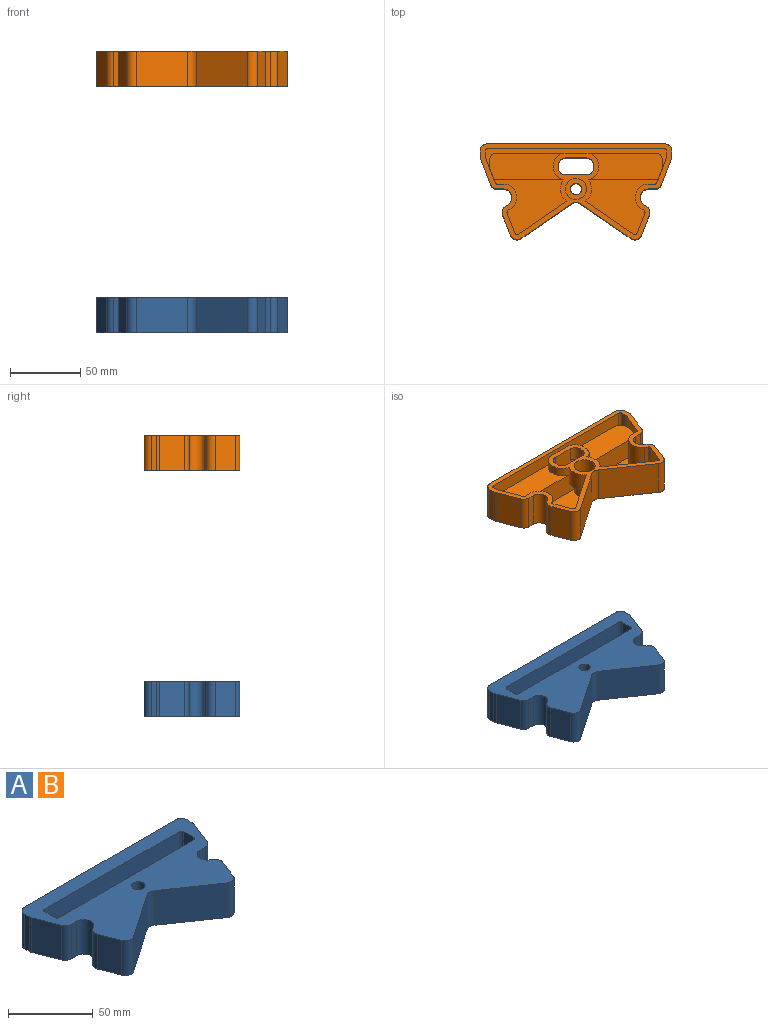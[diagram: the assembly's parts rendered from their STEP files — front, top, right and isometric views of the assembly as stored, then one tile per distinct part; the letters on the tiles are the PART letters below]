
ASSEMBLY  parts=2 mates=2
PART A: 100 faces, bbox 136x67.9x25 mm
  f0: plane 136x67.94mm, normal (0,0,-1), area 1747.5mm2, adj f3,f5,f6,f7,f8,f9,f11,f14
  f1: plane 50.5x12mm, normal (0,0,1), area 555mm2, adj f9,f10,f11,f39,f40,f42,f44,f46
  f2: cylinder r=4mm len=15mm, axis (0,0,-1), area 377mm2, adj f4,f36
  f3: plane 25x4.48mm, normal (0,-1,0), area 111.9mm2, adj f0,f4,f20,f28
  f4: plane 136x67.94mm, normal (0,0,1), area 5083.1mm2, adj f2,f3,f5,f6,f7,f8,f9,f10
  f5: plane 25x4.48mm, normal (0,-1,0), area 111.9mm2, adj f0,f4,f18,f25
  f6: plane 25x4.05mm, normal (1,0,0), area 101.4mm2, adj f0,f4,f31,f33
  f7: plane 126x25mm, normal (0,1,0), area 3150mm2, adj f0,f4,f33,f34
  f8: plane 25x4.05mm, normal (-1,0,0), area 101.4mm2, adj f0,f4,f32,f34
  f9: plane 112x25mm, normal (0,1,0), area 1830mm2, adj f0,f1,f4,f13,f38,f40,f45,f46
  f10: plane 15x8mm, normal (-1,0,0), area 120mm2, adj f1,f4,f39,f40
  f11: plane 112x25mm, normal (0,-1,0), area 1830mm2, adj f0,f1,f4,f13,f37,f39,f43,f44
  f12: plane 15x8mm, normal (1,0,0), area 120mm2, adj f4,f13,f37,f38
  f13: plane 50.5x12mm, normal (0,0,1), area 555mm2, adj f9,f11,f12,f37,f38,f41,f43,f45
  f14: plane 25x2.23mm, normal (-0.57,0.82,0), area 67.8mm2, adj f0,f4,f18,f26
  f15: plane 35.62x25mm, normal (0.57,-0.82,0), area 1081mm2, adj f0,f4,f19,f27
  f16: plane 35.62x25mm, normal (-0.57,-0.82,0), area 1081mm2, adj f0,f4,f19,f29
  f17: plane 25x2.23mm, normal (0.57,0.82,0), area 67.8mm2, adj f0,f4,f20,f30
  f18: cylinder r=6mm len=25mm, axis (0,0,-1), area 380.9mm2, adj f0,f4,f5,f14
  f19: cylinder r=6mm len=25mm, axis (0,0,1), area 180.8mm2, adj f0,f4,f15,f16
  f20: cylinder r=6mm len=25mm, axis (0,0,-1), area 380.9mm2, adj f0,f3,f4,f17
  f21: plane 25x14.34mm, normal (0.93,-0.37,0), area 385mm2, adj f0,f4,f29,f30
  f22: plane 25x14.34mm, normal (-0.93,-0.37,0), area 385mm2, adj f0,f4,f26,f27
  f23: plane 25x17.95mm, normal (-0.93,-0.37,0), area 481.9mm2, adj f0,f4,f25,f32
  f24: plane 25x17.95mm, normal (0.93,-0.37,0), area 481.9mm2, adj f0,f4,f28,f31
  f25: cylinder r=5mm len=25mm, axis (0,0,-1), area 149.6mm2, adj f0,f4,f5,f23
  f26: cylinder r=5mm len=25mm, axis (0,0,1), area 167.8mm2, adj f0,f4,f14,f22
  f27: cylinder r=5mm len=25mm, axis (0,0,-1), area 224.9mm2, adj f0,f4,f15,f22
  f28: cylinder r=5mm len=25mm, axis (0,0,1), area 149.6mm2, adj f0,f3,f4,f24
  f29: cylinder r=5mm len=25mm, axis (0,0,1), area 224.9mm2, adj f0,f4,f16,f21
  f30: cylinder r=5mm len=25mm, axis (0,0,-1), area 167.8mm2, adj f0,f4,f17,f21
  f31: cylinder r=5mm len=25mm, axis (0,0,-1), area 46.7mm2, adj f0,f4,f6,f24
  f32: cylinder r=5mm len=25mm, axis (0,0,1), area 46.7mm2, adj f0,f4,f8,f23
  f33: cylinder r=5mm len=25mm, axis (0,0,-1), area 196.3mm2, adj f0,f4,f6,f7
  f34: cylinder r=5mm len=25mm, axis (0,0,1), area 196.3mm2, adj f0,f4,f7,f8
  f35: cylinder r=7.5mm len=15mm, axis (0,0,-1), area 471.2mm2, adj f0,f36
  f36: plane 15x15mm, normal (0,0,-1), area 126.4mm2, adj f2,f35
  f37: cylinder r=2mm len=15mm, axis (0,0,-1), area 47.1mm2, adj f4,f11,f12,f13
  f38: cylinder r=2mm len=15mm, axis (0,0,1), area 47.1mm2, adj f4,f9,f12,f13
  f39: cylinder r=2mm len=15mm, axis (0,0,1), area 47.1mm2, adj f1,f4,f10,f11
  f40: cylinder r=2mm len=15mm, axis (0,0,-1), area 47.1mm2, adj f1,f4,f9,f10
  f41: plane 10x2mm, normal (1,0,0), area 20mm2, adj f0,f13,f43,f45
  f42: plane 10x2mm, normal (-1,0,0), area 20mm2, adj f0,f1,f44,f46
  f43: cylinder r=5mm len=10mm, axis (0,0,1), area 78.5mm2, adj f0,f11,f13,f41
  f44: cylinder r=5mm len=10mm, axis (0,0,-1), area 78.5mm2, adj f0,f1,f11,f42
  f45: cylinder r=5mm len=10mm, axis (0,0,-1), area 78.5mm2, adj f0,f9,f13,f41
  f46: cylinder r=5mm len=10mm, axis (0,0,1), area 78.5mm2, adj f0,f1,f9,f42
  f47: cylinder r=9.5mm len=8mm, axis (0,0,1), area 17.4mm2, adj f48,f55,f56,f70
  f48: plane 15.14x7.53mm, normal (0,0,1), area 56.8mm2, adj f47,f54,f55,f65,f70
  f49: plane 15.14x7.53mm, normal (0,0,1), area 56.8mm2, adj f50,f51,f58,f73,f89
  f50: plane 52.26x15mm, normal (0,-1,0), area 747.9mm2, adj f49,f52,f58,f60,f89,f93
  f51: plane 35.62x24.51mm, normal (0.57,0.82,0), area 906.4mm2, adj f0,f49,f60,f73,f83,f89
  f52: plane 54x19mm, normal (0,0,-1), area 874.4mm2, adj f50,f66,f67,f78,f89,f92,f93,f95
  f53: plane 54x19mm, normal (0,0,-1), area 874.4mm2, adj f54,f65,f67,f68,f77,f90,f91,f94
  f54: cylinder r=11mm len=15.24mm, axis (0,0,-1), area 228.9mm2, adj f0,f48,f53,f65,f70,f98
  f55: cylinder r=7.5mm len=13.15mm, axis (0,0,-1), area 128.3mm2, adj f47,f48,f56,f65
  f56: plane 54.9x39.47mm, normal (0,0,-1), area 1122.5mm2, adj f47,f55,f61,f65,f69,f70,f72,f76
  f57: plane 129x13.48mm, normal (0,0,-1), area 439mm2, adj f62,f63,f64,f66,f67,f68,f77,f78
  f58: cylinder r=7.5mm len=13.15mm, axis (0,0,-1), area 128.3mm2, adj f49,f50,f60,f73
  f59: plane 21.5x4.48mm, normal (0,1,0), area 96.2mm2, adj f0,f60,f74,f82
  f60: plane 54.9x39.47mm, normal (0,0,-1), area 1122.5mm2, adj f50,f51,f58,f59,f71,f73,f74,f75
  f61: plane 21.5x4.48mm, normal (0,1,0), area 96.2mm2, adj f0,f56,f72,f79
  f62: plane 21.5x4.05mm, normal (-1,0,0), area 87.2mm2, adj f0,f57,f85,f87
  f63: plane 126x21.5mm, normal (0,-1,0), area 2709mm2, adj f0,f57,f87,f88
  f64: plane 21.5x4.05mm, normal (1,0,0), area 87.2mm2, adj f0,f57,f86,f88
  f65: plane 52.26x15mm, normal (0,-1,0), area 747.9mm2, adj f48,f53,f54,f55,f56,f91
  f66: plane 15x4.98mm, normal (1,0,0), area 74.8mm2, adj f52,f57,f78,f92
  f67: plane 112x21.5mm, normal (0,1,0), area 1777.5mm2, adj f0,f52,f53,f57,f90,f92,f96,f97
  f68: plane 15x4.98mm, normal (-1,0,0), area 74.8mm2, adj f53,f57,f77,f90
  f69: plane 21.5x2.23mm, normal (0.57,-0.82,0), area 58.3mm2, adj f0,f56,f72,f80
  f70: plane 35.62x24.51mm, normal (-0.57,0.82,0), area 906.4mm2, adj f0,f47,f48,f54,f56,f81
  f71: plane 21.5x2.23mm, normal (-0.57,-0.82,0), area 58.3mm2, adj f0,f60,f74,f84
  f72: cylinder r=9.5mm len=21.5mm, axis (0,0,-1), area 518.6mm2, adj f0,f56,f61,f69
  f73: cylinder r=9.5mm len=8mm, axis (0,0,1), area 17.4mm2, adj f49,f51,f58,f60
  f74: cylinder r=9.5mm len=21.5mm, axis (0,0,-1), area 518.6mm2, adj f0,f59,f60,f71
  f75: plane 21.5x14.34mm, normal (-0.93,0.37,0), area 331.1mm2, adj f0,f60,f83,f84
  f76: plane 21.5x14.34mm, normal (0.93,0.37,0), area 331.1mm2, adj f0,f56,f80,f81
  f77: plane 21.5x17.95mm, normal (0.93,0.37,0), area 285.9mm2, adj f0,f53,f56,f57,f68,f79,f86,f91
  f78: plane 21.5x17.95mm, normal (-0.93,0.37,0), area 285.9mm2, adj f0,f52,f57,f60,f66,f82,f85,f93
  f79: cylinder r=1.5mm len=21.5mm, axis (0,0,-1), area 38.6mm2, adj f0,f56,f61,f77
  f80: cylinder r=1.5mm len=21.5mm, axis (0,0,1), area 43.3mm2, adj f0,f56,f69,f76
  f81: cylinder r=1.5mm len=21.5mm, axis (0,0,-1), area 58mm2, adj f0,f56,f70,f76
  f82: cylinder r=1.5mm len=21.5mm, axis (0,0,1), area 38.6mm2, adj f0,f59,f60,f78
  f83: cylinder r=1.5mm len=21.5mm, axis (0,0,1), area 58mm2, adj f0,f51,f60,f75
  f84: cylinder r=1.5mm len=21.5mm, axis (0,0,-1), area 43.3mm2, adj f0,f60,f71,f75
  f85: cylinder r=1.5mm len=21.5mm, axis (0,0,-1), area 12.1mm2, adj f0,f57,f62,f78
  f86: cylinder r=1.5mm len=21.5mm, axis (0,0,1), area 12.1mm2, adj f0,f57,f64,f77
  f87: cylinder r=1.5mm len=21.5mm, axis (0,0,-1), area 50.7mm2, adj f0,f57,f62,f63
  f88: cylinder r=1.5mm len=21.5mm, axis (0,0,1), area 50.7mm2, adj f0,f57,f63,f64
  f89: cylinder r=11mm len=15.24mm, axis (0,0,-1), area 228.9mm2, adj f0,f49,f50,f51,f52,f99
  f90: cylinder r=5.5mm len=15mm, axis (0,0,-1), area 129.6mm2, adj f53,f57,f67,f68
  f91: cylinder r=5.5mm len=15mm, axis (0,0,1), area 36.7mm2, adj f53,f56,f65,f77
  f92: cylinder r=5.5mm len=15mm, axis (0,0,1), area 129.6mm2, adj f52,f57,f66,f67
  f93: cylinder r=5.5mm len=15mm, axis (0,0,-1), area 36.7mm2, adj f50,f52,f60,f78
  f94: plane 6.5x2mm, normal (-1,0,0), area 13mm2, adj f0,f53,f96,f98
  f95: plane 6.5x2mm, normal (1,0,0), area 13mm2, adj f0,f52,f97,f99
  f96: cylinder r=8.5mm len=8.5mm, axis (0,0,1), area 86.8mm2, adj f0,f53,f67,f94
  f97: cylinder r=8.5mm len=8.5mm, axis (0,0,-1), area 86.8mm2, adj f0,f52,f67,f95
  f98: cylinder r=8.5mm len=8.4mm, axis (0,0,-1), area 78.3mm2, adj f0,f53,f54,f94
  f99: cylinder r=8.5mm len=8.4mm, axis (0,0,1), area 78.3mm2, adj f0,f52,f89,f95
PART B: same geometry as A
PLACE A at identity fixed
PLACE B rot(axis=(0,1,0),180deg) t=(0,0,200)mm
MATE planar A.f2 <-> B.f2  axis (0,0,1) through (0,0,25)mm
MATE planar A.f23 <-> B.f24  axis (-0.93,-0.37,0) through (-64.13,12.15,12.5)mm
